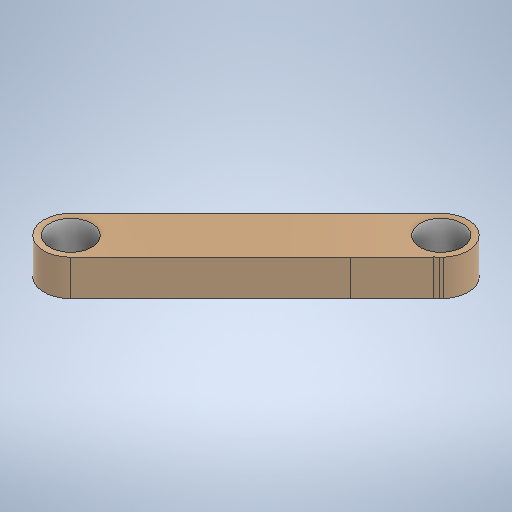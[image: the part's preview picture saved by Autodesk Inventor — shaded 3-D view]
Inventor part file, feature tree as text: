
AUTODESK INVENTOR PART (.ipt)
format: ipt  version: 2025.1 (Build 291241000, 241)  size: 331,264 bytes
history: native  units: in
note: dims shown in document units (in); Inventor stores cm internally (conversion verified against a paired STEP export)
features: extrude x2, sketch x2, other x2
ambient origin geometry x8: Origin, YZ Plane, XZ Plane, XY Plane, X Axis, Y Axis, Z Axis, Center Point
bodies: Solid1 (feature_tree)
feature tree (6):
  extrude  "Extrusion1"  Depth=0.3937in
  extrude  "Extrusion2"  Depth=0.1181in
  sketch  "Sketch1"  dims[d0=0.3346in d1=0.3346in d2=0.3346in d3=0.3346in d4=0.1181in d5=0.1181in d6=0.1181in d7=0.1181in]
  sketch  "Sketch2"  dims[d8=1.0in d9=1.0in d10=2.0in d11=2.0in d12=0.4331in d13=0.4331in d14=0.4331in d15=0.4331in d16=0.4331in d17=0.4331in d18=0.4331in d19=0.4331in d20=0.4331in d21=2.7559in d22=0.1969in d23=0.1969in d24=0.67in d25=0.1181in d26=0.4331in d28=0.1772in d30=0.1181in d31=0.0in d33=0.1181in d34=0.1772in d35=0.1378in d36=0.1378in d37=0.3937in d38=0.0in]
  other  "Finish1"
  other  "Finish2"
